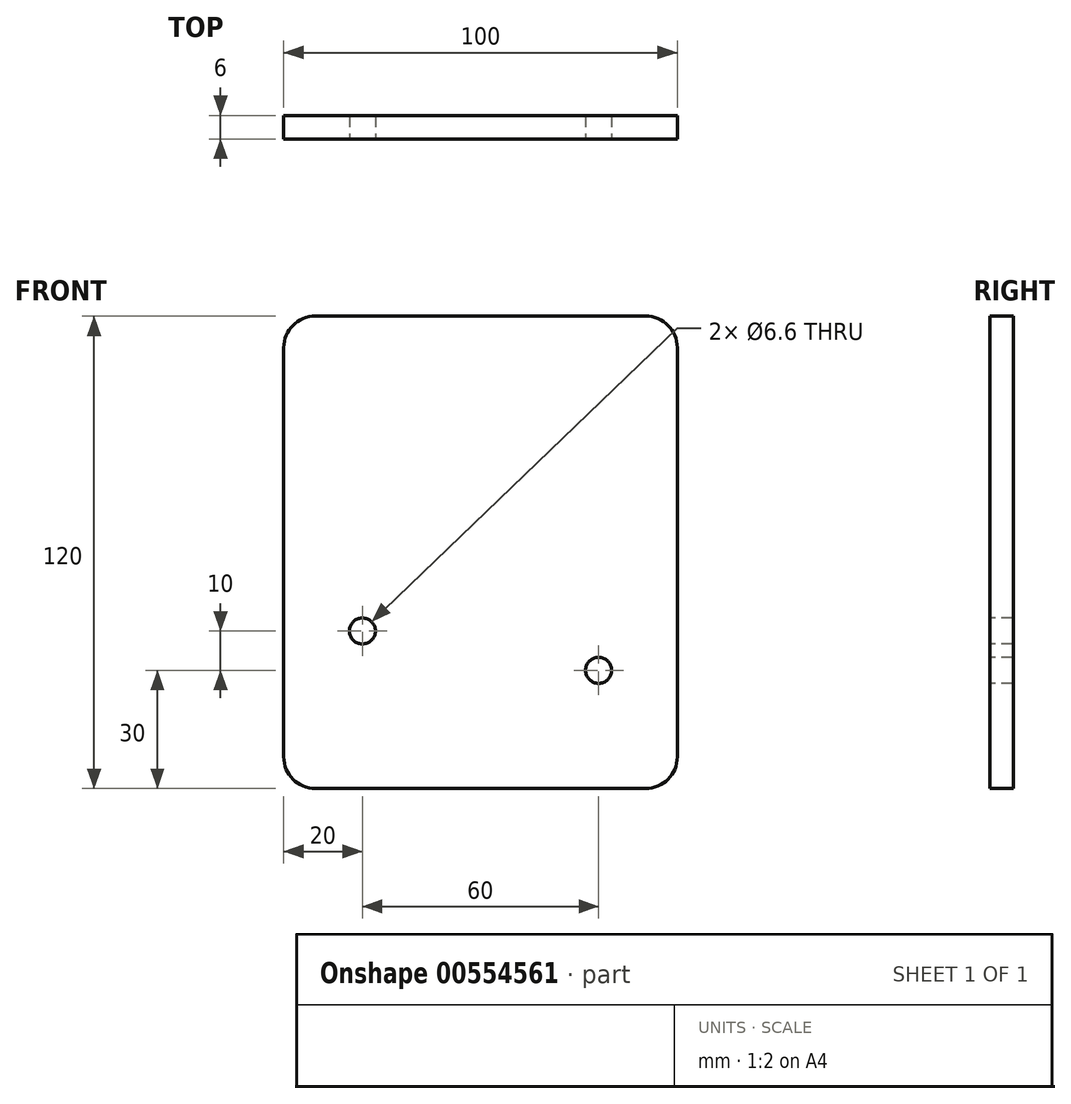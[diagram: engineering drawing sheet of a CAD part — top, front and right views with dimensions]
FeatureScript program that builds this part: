
annotation { "Feature Type Name" : "Feature", "Feature Type Description" : "" }
export const myFeature = defineFeature(function(context is Context, id is Id, definition is map)
    precondition{}
    {
        {
            var Q0;
            Q0=qCreatedBy(makeId("Front.planeOp"),FACE);
            var sketch = newSketch(context, id + "F0", { "sketchPlane" : qUnion([Q0])});
            skLineSegment(sketch, "E0.bottom", {"start": v(0, 0) * mm, "end": v(100, 0) * mm});
            skLineSegment(sketch, "E0.top", {"start": v(0, 120) * mm, "end": v(100, 120) * mm});
            skLineSegment(sketch, "E0.left", {"start": v(0, 0) * mm, "end": v(0, 120) * mm});
            skLineSegment(sketch, "E0.right", {"start": v(100, 0) * mm, "end": v(100, 120) * mm});
            skSolve(sketch);
        }
        {
            var Q0;
            Q0 = qSketchRegion(id + "F0", true);
            var Q1;
            Q1=makeQuery(id+"F0.imprint","IMPRINT",FACE,{"disambiguationData":[TD([[makeQuery(id+"F0.imprint","IMPRINT",EDGE,{"derivedFrom":sQuery(id+"F0.wireOp",EDGE,"E0.bottom")}),1.0]])]});
            extrude(context, id + "F1", {"entities" : qUnion([Q0, Q1]), "depth" : 6 * mm, "offsetDistance" : 25 * mm});
        }
        {
            var Q0;
            Q0=makeQuery(id+"F1.opExtrude","CAP_FACE",FACE,{"disambiguationData":[OSD([sQuery(id+"F0.wireOp",EDGE,"E0.bottom"),sQuery(id+"F0.wireOp",EDGE,"E0.top"),sQuery(id+"F0.wireOp",EDGE,"E0.left"),sQuery(id+"F0.wireOp",EDGE,"E0.right")])],"isStart":false});
            var sketch = newSketch(context, id + "F2", { "sketchPlane" : qUnion([Q0])});
            skPoint(sketch, "E1", {"position": v(80, 30) * mm});
            skPoint(sketch, "E2", {"position": v(20, 40) * mm});
            skSolve(sketch);
        }
        {
            var Q0;
            Q0=sQuery(id+"F2.wireOp",VERTEX,"E1");
            var Q1;
            Q1=sQuery(id+"F2.wireOp",VERTEX,"E2");
            var Q2;
            Q2=makeQuery(id+"F1.opExtrude","SWEPT_BODY",BODY,{"disambiguationData":[OSD([sQuery(id+"F0.wireOp",EDGE,"E0.bottom"),sQuery(id+"F0.wireOp",EDGE,"E0.top"),sQuery(id+"F0.wireOp",EDGE,"E0.left"),sQuery(id+"F0.wireOp",EDGE,"E0.right")])]});
            hole(context, id + "F3", {"style" : HoleStyle.SIMPLE, "endStyle" : HoleEndStyle.THROUGH, "standardTappedOrClearance" : lookupTablePath({ "standard" : "ISO", "fit" : "Normal", "size" : "M6", "type" : "Clearance" }), "standardBlindInLast" : lookupTablePath({ "fit" : "Standard", "standard" : "ISO", "size" : "M6", "type" : "Clearance" }), "holeDiameter" : 6.6 * mm, "isTappedThrough" : true, "tappedDepth" : 8 * mm, "tapClearance" : 3, "startFromSketch" : true, "locations" : qUnion([Q0, Q1]), "scope" : qUnion([Q2])});
        }
        {
            var Q0;
            Q0=makeQuery(id+"F1.opExtrude","SWEPT_EDGE",EDGE,{"disambiguationData":[OSD([sQuery(id+"F0.wireOp",EDGE,"E0.top"),sQuery(id+"F0.wireOp",EDGE,"E0.right")])]});
            var Q1;
            Q1=makeQuery(id+"F1.opExtrude","SWEPT_EDGE",EDGE,{"disambiguationData":[OSD([sQuery(id+"F0.wireOp",EDGE,"E0.bottom"),sQuery(id+"F0.wireOp",EDGE,"E0.right")])]});
            var Q2;
            Q2=makeQuery(id+"F1.opExtrude","SWEPT_EDGE",EDGE,{"disambiguationData":[OSD([sQuery(id+"F0.wireOp",EDGE,"E0.bottom"),sQuery(id+"F0.wireOp",EDGE,"E0.left")])]});
            var Q3;
            Q3=makeQuery(id+"F1.opExtrude","SWEPT_EDGE",EDGE,{"disambiguationData":[OSD([sQuery(id+"F0.wireOp",EDGE,"E0.top"),sQuery(id+"F0.wireOp",EDGE,"E0.left")])]});
            fillet(context, id + "F4", {"entities" : qUnion([Q0, Q1, Q2, Q3]), "radius" : 8 * mm, "tangentPropagation" : true, "allowEdgeOverflow" : false});
        }
    });
